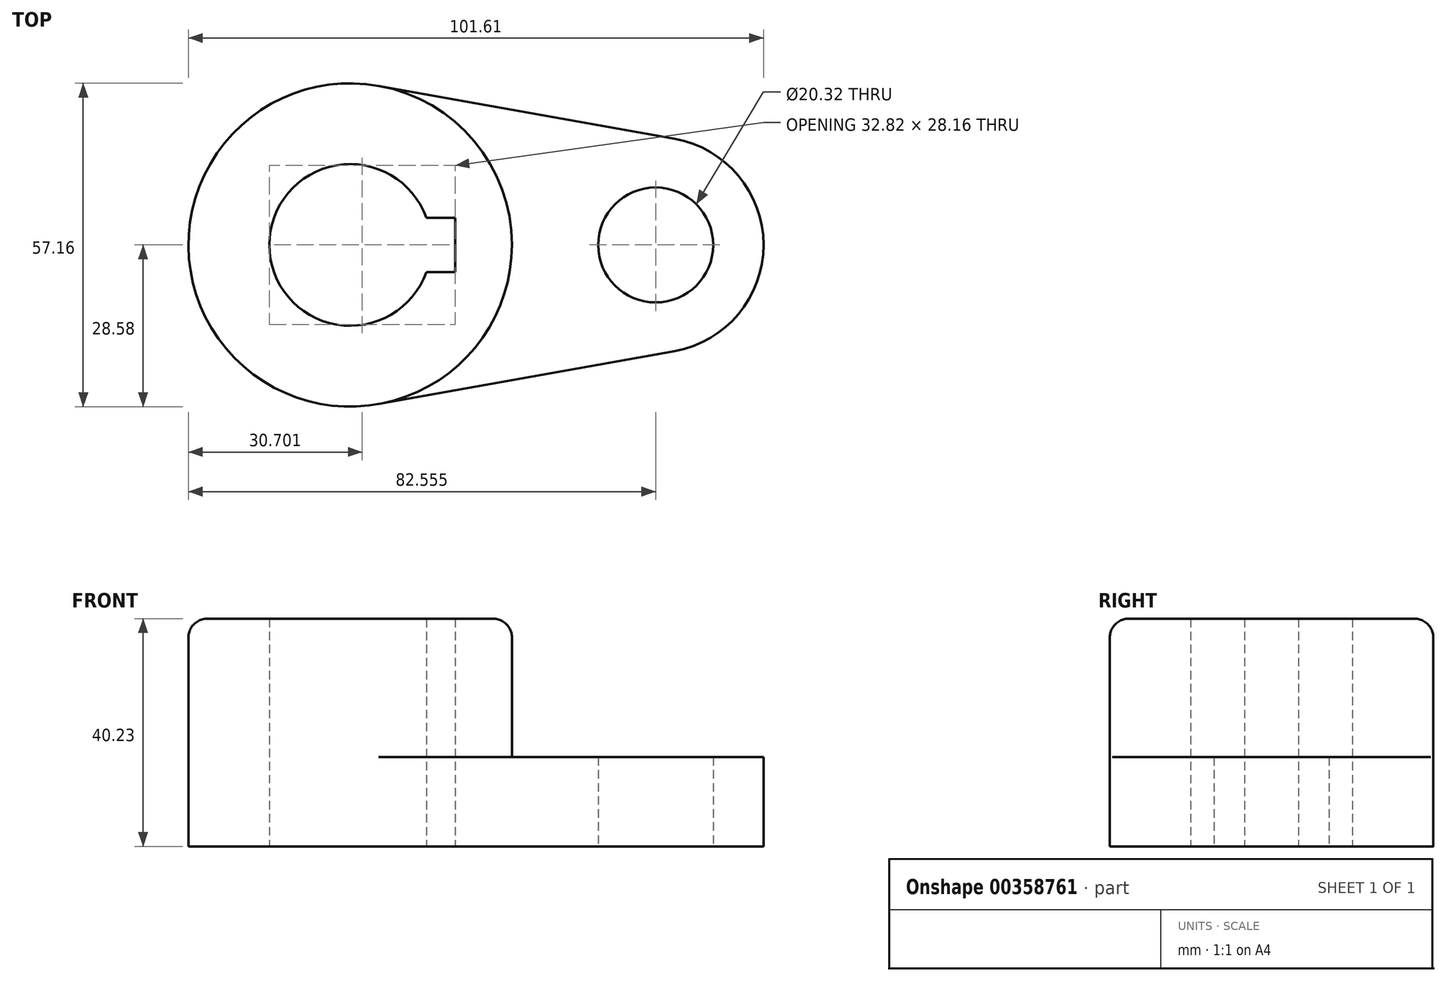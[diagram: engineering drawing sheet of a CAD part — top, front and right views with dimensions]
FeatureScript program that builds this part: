
annotation { "Feature Type Name" : "Feature", "Feature Type Description" : "" }
export const myFeature = defineFeature(function(context is Context, id is Id, definition is map)
    precondition{}
    {
        {
            var Q0;
            Q0=qCreatedBy(makeId("Top.planeOp"),FACE);
            var sketch = newSketch(context, id + "F0", { "sketchPlane" : qUnion([Q0])});
            skCircle(sketch, "E0", {"center": v(0, 0) * mm, "radius": 28.58 * mm});
            skArc(sketch, "E1", {"start": v(13.46, 4.8) * mm, "mid": v(-14.29, 0) * mm, "end": v(13.46, -4.8) * mm});
            skLineSegment(sketch, "E2", {"start": v(-66.14, 0) * mm, "end": v(59.21, 0) * mm, "construction": true});
            skLineSegment(sketch, "E3.0", {"start": v(18.53, -0.04) * mm, "end": v(18.53, 4.8) * mm});
            skLineSegment(sketch, "E4.0", {"start": v(18.53, 4.8) * mm, "end": v(13.46, 4.8) * mm});
            skLineSegment(sketch, "E5.MirrorCS", {"start": v(18.53, -4.8) * mm, "end": v(13.46, -4.8) * mm});
            skLineSegment(sketch, "E6.MirrorCS", {"start": v(18.53, 0.04) * mm, "end": v(18.53, -4.8) * mm});
            skSolve(sketch);
        }
        {
            var Q0;
            Q0 = qSketchRegion(id + "F0", true);
            extrude(context, id + "F1", {"entities" : qUnion([Q0]), "depth" : 40.23 * mm});
        }
        {
            var Q0;
            Q0=qCreatedBy(makeId("Top.planeOp"),FACE);
            var sketch = newSketch(context, id + "F2", { "sketchPlane" : qUnion([Q0])});
            skCircle(sketch, "E7", {"center": v(53.98, 0) * mm, "radius": 10.16 * mm});
            skArc(sketch, "E8", {"start": v(57.34, -18.75) * mm, "mid": v(73.03, 0) * mm, "end": v(57.34, 18.75) * mm});
            skCircle(sketch, "E9.0", {"center": v(0, 0) * mm, "radius": 28.58 * mm});
            skLineSegment(sketch, "E10", {"start": v(57.34, -18.75) * mm, "end": v(5.04, -28.13) * mm});
            skLineSegment(sketch, "E11", {"start": v(57.34, 18.75) * mm, "end": v(5.04, 28.13) * mm});
            skSolve(sketch);
        }
        {
            var Q0;
            Q0=makeQuery(id+"F2.imprint","IMPRINT",FACE,{"disambiguationData":[TD([[makeQuery(id+"F2.imprint","IMPRINT",EDGE,{"derivedFrom":sQuery(id+"F2.wireOp",EDGE,"E7")}),-1.0]])]});
            extrude(context, id + "F3", {"entities" : qUnion([Q0]), "operationType" : NewBodyOperationType.ADD, "depth" : 15.77 * mm});
        }
        {
            var Q0;
            Q0=makeQuery(id+"F1.opExtrude","CAP_EDGE",EDGE,{"disambiguationData":[OSD([sQuery(id+"F0.wireOp",EDGE,"E0")])],"isStart":false});
            fillet(context, id + "F4", {"entities" : qUnion([Q0]), "radius" : 3.3 * mm, "tangentPropagation" : true, "allowEdgeOverflow" : false});
        }
    });
